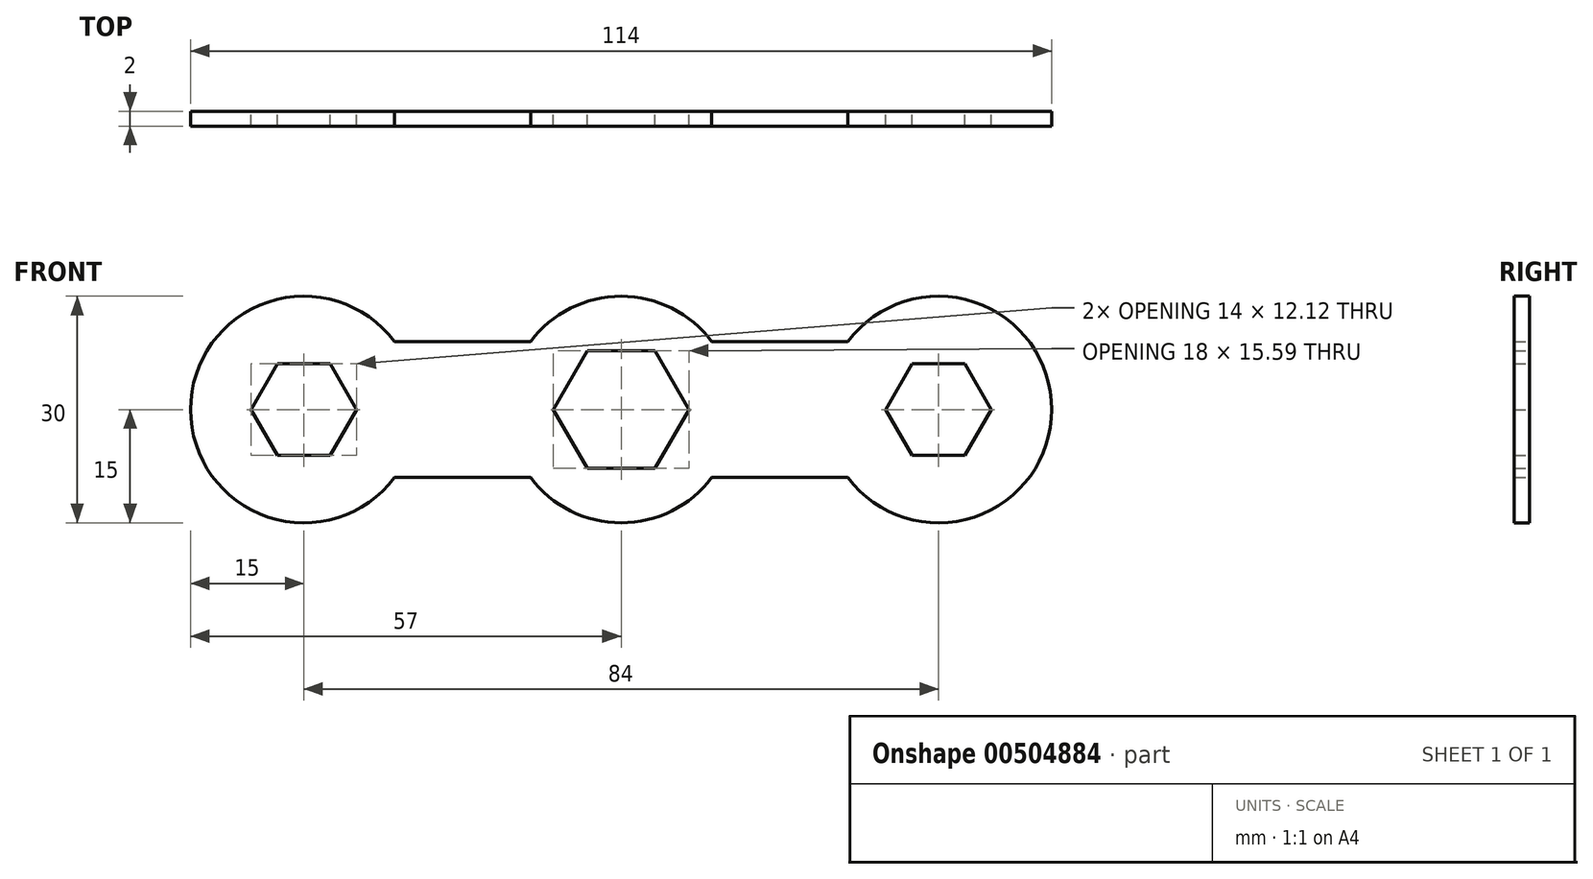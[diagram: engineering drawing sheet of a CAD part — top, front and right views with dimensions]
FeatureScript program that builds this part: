
annotation { "Feature Type Name" : "Feature", "Feature Type Description" : "" }
export const myFeature = defineFeature(function(context is Context, id is Id, definition is map)
    precondition{}
    {
        {
            var Q0;
            Q0=qCreatedBy(makeId("Front.planeOp"),FACE);
            var sketch = newSketch(context, id + "F0", { "sketchPlane" : qUnion([Q0])});
            skLineSegment(sketch, "E0.bottom", {"start": v(30, 9) * mm, "end": v(12, 9) * mm});
            skLineSegment(sketch, "E0.top", {"start": v(30, -9) * mm, "end": v(12, -9) * mm});
            skPoint(sketch, "E0.middle", {"position": v(0, 0) * mm});
            skArc(sketch, "E1", {"start": v(12, 9) * mm, "mid": v(0, 15) * mm, "end": v(-12, 9) * mm});
            skArc(sketch, "E2", {"start": v(-30, 9) * mm, "mid": v(-57, 0) * mm, "end": v(-30, -9) * mm});
            skArc(sketch, "E3", {"start": v(30, -9) * mm, "mid": v(57, 0) * mm, "end": v(30, 9) * mm});
            skCircle(sketch, "E4.cCircle", {"center": v(-42, 0) * mm, "radius": 6.06 * mm, "construction": true});
            skLineSegment(sketch, "E4.0", {"start": v(-38.5, 6.06) * mm, "end": v(-35, 0) * mm});
            skLineSegment(sketch, "E4.1", {"start": v(-35, 0) * mm, "end": v(-38.5, -6.06) * mm});
            skLineSegment(sketch, "E4.2", {"start": v(-38.5, -6.06) * mm, "end": v(-45.5, -6.06) * mm});
            skLineSegment(sketch, "E4.3", {"start": v(-45.5, -6.06) * mm, "end": v(-49, 0) * mm});
            skLineSegment(sketch, "E4.4", {"start": v(-49, 0) * mm, "end": v(-45.5, 6.06) * mm});
            skLineSegment(sketch, "E4.5", {"start": v(-45.5, 6.06) * mm, "end": v(-38.5, 6.06) * mm});
            skPoint(sketch, "E4.0.midPoint", {"position": v(-36.75, 3.03) * mm});
            skCircle(sketch, "E5.cCircle", {"center": v(42, 0) * mm, "radius": 6.06 * mm, "construction": true});
            skLineSegment(sketch, "E5.0", {"start": v(45.5, 6.06) * mm, "end": v(49, 0) * mm});
            skLineSegment(sketch, "E5.1", {"start": v(49, 0) * mm, "end": v(45.5, -6.06) * mm});
            skLineSegment(sketch, "E5.2", {"start": v(45.5, -6.06) * mm, "end": v(38.5, -6.06) * mm});
            skLineSegment(sketch, "E5.3", {"start": v(38.5, -6.06) * mm, "end": v(35, 0) * mm});
            skLineSegment(sketch, "E5.4", {"start": v(35, 0) * mm, "end": v(38.5, 6.06) * mm});
            skLineSegment(sketch, "E5.5", {"start": v(38.5, 6.06) * mm, "end": v(45.5, 6.06) * mm});
            skPoint(sketch, "E5.0.midPoint", {"position": v(47.25, 3.03) * mm});
            skCircle(sketch, "E6.cCircle", {"center": v(0, 0) * mm, "radius": 7.8 * mm, "construction": true});
            skLineSegment(sketch, "E6.0", {"start": v(4.5, 7.8) * mm, "end": v(9, 0) * mm});
            skLineSegment(sketch, "E6.1", {"start": v(9, 0) * mm, "end": v(4.5, -7.8) * mm});
            skLineSegment(sketch, "E6.2", {"start": v(4.5, -7.8) * mm, "end": v(-4.5, -7.8) * mm});
            skLineSegment(sketch, "E6.3", {"start": v(-4.5, -7.8) * mm, "end": v(-9, 0) * mm});
            skLineSegment(sketch, "E6.4", {"start": v(-9, 0) * mm, "end": v(-4.5, 7.8) * mm});
            skLineSegment(sketch, "E6.5", {"start": v(-4.5, 7.8) * mm, "end": v(4.5, 7.8) * mm});
            skPoint(sketch, "E6.0.midPoint", {"position": v(6.75, 3.9) * mm});
            skPoint(sketch, "E7.orphan", {"position": v(42, 9) * mm});
            skPoint(sketch, "E0.left.end.orphan", {"position": v(42, -9) * mm});
            skArc(sketch, "E8.trimOffspring", {"start": v(-12, -9) * mm, "mid": v(0, -15) * mm, "end": v(12, -9) * mm});
            skPoint(sketch, "E9.orphan", {"position": v(-42, 9) * mm});
            skPoint(sketch, "E10.orphan", {"position": v(-42, -9) * mm});
            skLineSegment(sketch, "E11.trimOffspring", {"start": v(-12, -9) * mm, "end": v(-30, -9) * mm});
            skLineSegment(sketch, "E12.trimOffspring", {"start": v(-12, 9) * mm, "end": v(-30, 9) * mm});
            skSolve(sketch);
        }
        {
            var Q0;
            Q0 = qSketchRegion(id + "F0", true);
            var Q1;
            Q1 = qConstructionFilter(qBodyType(qCreatedBy(id + "F0" ,EDGE), BodyType.WIRE), ConstructionObject.NO);
            extrude(context, id + "F1", {"entities" : qUnion([Q0]), "surfaceEntities" : qUnion([Q1]), "depth" : 2 * mm});
        }
    });
